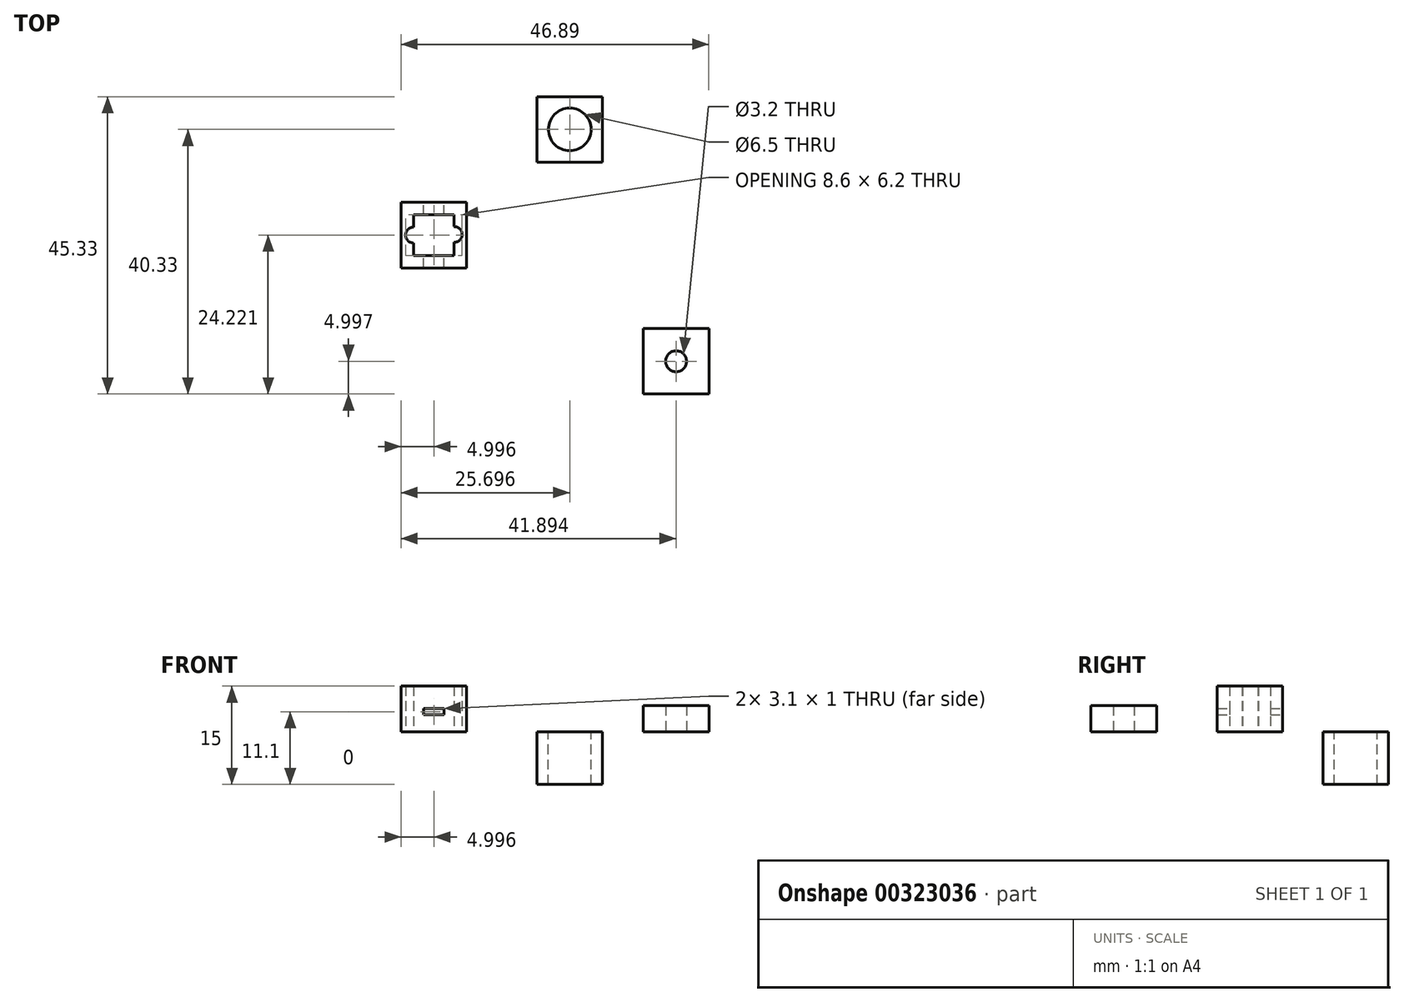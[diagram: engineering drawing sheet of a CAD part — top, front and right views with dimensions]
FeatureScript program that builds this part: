
annotation { "Feature Type Name" : "Feature", "Feature Type Description" : "" }
export const myFeature = defineFeature(function(context is Context, id is Id, definition is map)
    precondition{}
    {
        {
            var Q0;
            Q0=qCreatedBy(makeId("Top.planeOp"),FACE);
            var sketch = newSketch(context, id + "F0", { "sketchPlane" : qUnion([Q0])});
            skLineSegment(sketch, "E0.bottom", {"start": v(-17.71, -4.14) * mm, "end": v(-7.71, -4.14) * mm});
            skLineSegment(sketch, "E0.top", {"start": v(-17.71, -14.14) * mm, "end": v(-7.71, -14.14) * mm});
            skLineSegment(sketch, "E0.left", {"start": v(-17.71, -4.14) * mm, "end": v(-17.71, -14.14) * mm});
            skLineSegment(sketch, "E0.right", {"start": v(-7.71, -4.14) * mm, "end": v(-7.71, -14.14) * mm});
            skLineSegment(sketch, "E1.bottom", {"start": v(-15.81, -6.04) * mm, "end": v(-9.61, -6.04) * mm});
            skLineSegment(sketch, "E1.top", {"start": v(-15.81, -12.24) * mm, "end": v(-9.61, -12.24) * mm});
            skLineSegment(sketch, "E1.left", {"start": v(-15.81, -6.04) * mm, "end": v(-15.81, -12.24) * mm});
            skLineSegment(sketch, "E1.right", {"start": v(-9.61, -6.04) * mm, "end": v(-9.61, -12.24) * mm});
            skArc(sketch, "E2", {"start": v(-15.81, -7.94) * mm, "mid": v(-17.01, -9.14) * mm, "end": v(-15.81, -10.34) * mm});
            skArc(sketch, "E3", {"start": v(-9.61, -10.24) * mm, "mid": v(-8.41, -9.04) * mm, "end": v(-9.61, -7.84) * mm});
            skSolve(sketch);
        }
        {
            var Q0;
            Q0=qCreatedBy(makeId("Top.planeOp"),FACE);
            var sketch = newSketch(context, id + "F1", { "sketchPlane" : qUnion([Q0])});
            skLineSegment(sketch, "E4.bottom", {"start": v(2.99, 11.97) * mm, "end": v(12.99, 11.97) * mm});
            skLineSegment(sketch, "E4.top", {"start": v(2.99, 1.97) * mm, "end": v(12.99, 1.97) * mm});
            skLineSegment(sketch, "E4.left", {"start": v(2.99, 11.97) * mm, "end": v(2.99, 1.97) * mm});
            skLineSegment(sketch, "E4.right", {"start": v(12.99, 11.97) * mm, "end": v(12.99, 1.97) * mm});
            skCircle(sketch, "E5", {"center": v(7.99, 6.97) * mm, "radius": 3.25 * mm});
            skSolve(sketch);
        }
        {
            var Q0;
            Q0=qCreatedBy(makeId("Top.planeOp"),FACE);
            var sketch = newSketch(context, id + "F2", { "sketchPlane" : qUnion([Q0])});
            skLineSegment(sketch, "E6.bottom", {"start": v(19.18, -23.36) * mm, "end": v(29.18, -23.36) * mm});
            skLineSegment(sketch, "E6.top", {"start": v(19.18, -33.36) * mm, "end": v(29.18, -33.36) * mm});
            skLineSegment(sketch, "E6.left", {"start": v(19.18, -23.36) * mm, "end": v(19.18, -33.36) * mm});
            skLineSegment(sketch, "E6.right", {"start": v(29.18, -23.36) * mm, "end": v(29.18, -33.36) * mm});
            skCircle(sketch, "E7", {"center": v(24.18, -28.36) * mm, "radius": 1.6 * mm});
            skSolve(sketch);
        }
        {
            var Q0;
            Q0=makeQuery(id+"F1.imprint","IMPRINT",FACE,{"disambiguationData":[TD([[makeQuery(id+"F1.imprint","IMPRINT",EDGE,{"derivedFrom":sQuery(id+"F1.wireOp",EDGE,"E4.bottom")}),-1.0]])]});
            extrude(context, id + "F3", {"entities" : qUnion([Q0]), "oppositeDirection" : true, "depth" : 8 * mm});
        }
        {
            var Q0;
            Q0=makeQuery(id+"F0.imprint","IMPRINT",FACE,{"disambiguationData":[TD([[makeQuery(id+"F0.imprint","IMPRINT",EDGE,{"derivedFrom":sQuery(id+"F0.wireOp",EDGE,"E0.bottom")}),-1.0]])]});
            extrude(context, id + "F4", {"entities" : qUnion([Q0]), "depth" : 7 * mm});
        }
        {
            var Q0;
            Q0=qCreatedBy(makeId("Front.planeOp"),FACE);
            var sketch = newSketch(context, id + "F5", { "sketchPlane" : qUnion([Q0])});
            skLineSegment(sketch, "E8.bottom", {"start": v(-14.26, 3.6) * mm, "end": v(-11.16, 3.6) * mm});
            skLineSegment(sketch, "E8.top", {"start": v(-14.26, 2.6) * mm, "end": v(-11.16, 2.6) * mm});
            skLineSegment(sketch, "E8.left", {"start": v(-14.26, 3.6) * mm, "end": v(-14.26, 2.6) * mm});
            skLineSegment(sketch, "E8.right", {"start": v(-11.16, 3.6) * mm, "end": v(-11.16, 2.6) * mm});
            skSolve(sketch);
        }
        {
            var Q0;
            Q0 = qSketchRegion(id + "F5", true);
            extrude(context, id + "F6", {"entities" : qUnion([Q0]), "operationType" : NewBodyOperationType.REMOVE, "endBound" : BoundingType.THROUGH_ALL, "depth" : 25 * mm});
        }
        {
            var Q0;
            Q0=makeQuery(id+"F2.imprint","IMPRINT",FACE,{"disambiguationData":[TD([[makeQuery(id+"F2.imprint","IMPRINT",EDGE,{"derivedFrom":sQuery(id+"F2.wireOp",EDGE,"E6.bottom")}),-1.0]])]});
            extrude(context, id + "F7", {"entities" : qUnion([Q0]), "depth" : 4 * mm});
        }
    });
